# Revit family: 52501-presto
name_source: partatom
category: Plumbing Fixtures
units: mm (PartAtom-declared; Revit-internal decimal feet)

## family parameters
Always vertical = Yes
Cut with Voids When Loaded = No
Maintain Annotation Orientation = No
OmniClass Number = 23.45.00.00
OmniClass Title = Sanitary, Laundry, and Cleaning Equipment
Part Type = Normal
Room Calculation Point = No
Round Connector Dimension = Use Diameter
Shared = No
Work Plane-Based = Yes

## types (1)
- 52501-presto
    - Hydraulic supply = 15 "
    > Thermal resistance : = 75.0000 (h·ft²·°F)/BTU
    Default Elevation = 1219 mm
    Description = Modular detection
    Manufacturer = presto
    Model = 52501
    Recommended pressure = 3.00 bar
    URL = https://www.prestodatashare.com
    brand = Les Robinets PRESTO
    flow = 6 L/min
    flow time = 15.0 s
    glass = Default
    material = stain
    min pressure = 1.00 bar
    pressure = 5.00 bar
    range = Modular detection
    ref = 52501 - Modular sensor detection for shower, cross-partition 1-30mm, 30sec, 6l/min, mains

## geometry (parser evidence)
native form markers: Sweep x3
no freeform markers — native parametric forms only
